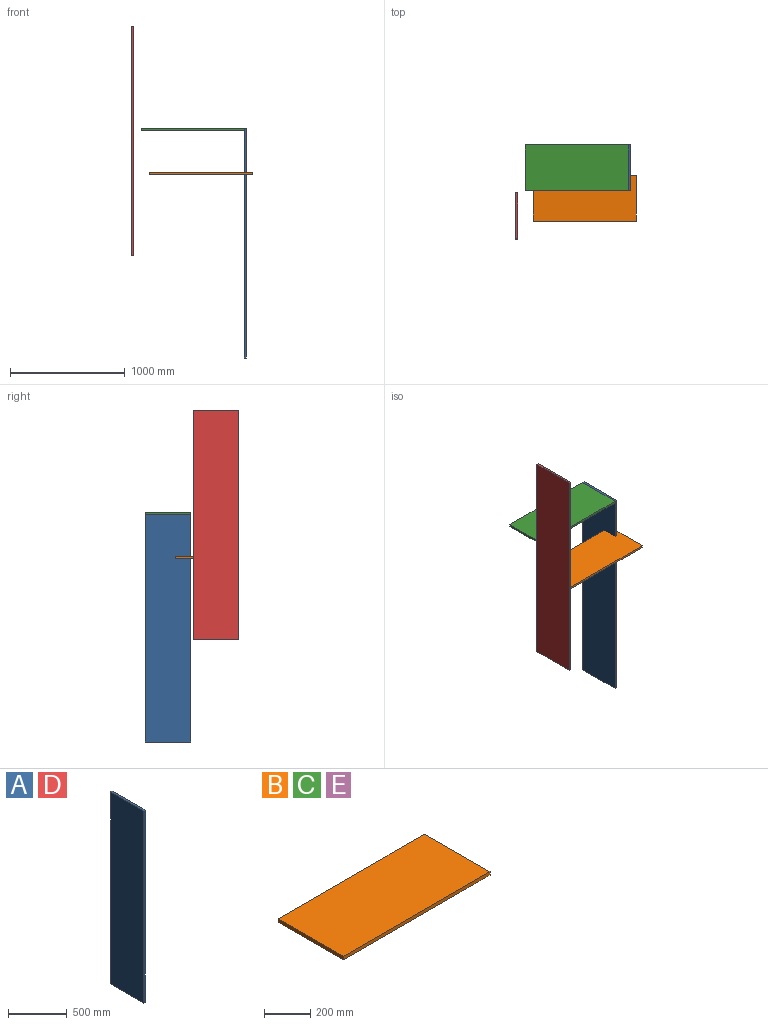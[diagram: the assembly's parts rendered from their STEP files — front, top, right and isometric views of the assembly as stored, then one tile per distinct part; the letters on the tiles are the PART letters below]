
ASSEMBLY  parts=5 mates=1
PART A: 6 faces, bbox 18x400x2000 mm
  f0: plane 2000x400mm, normal (1,0,0), area 800000mm2, adj f1,f3,f4,f5
  f1: plane 400x18mm, normal (0,0,1), area 7200mm2, adj f0,f2,f4,f5
  f2: plane 2000x400mm, normal (-1,0,0), area 800000mm2, adj f1,f3,f4,f5
  f3: plane 400x18mm, normal (0,0,-1), area 7200mm2, adj f0,f2,f4,f5
  f4: plane 2000x18mm, normal (0,-1,0), area 36000mm2, adj f0,f1,f2,f3
  f5: plane 2000x18mm, normal (0,1,0), area 36000mm2, adj f0,f1,f2,f3
PART B: 6 faces, bbox 900x400x18 mm
  f0: plane 900x400mm, normal (0,0,1), area 360000mm2, adj f1,f3,f4,f5
  f1: plane 400x18mm, normal (-1,0,0), area 7200mm2, adj f0,f2,f4,f5
  f2: plane 900x400mm, normal (0,0,-1), area 360000mm2, adj f1,f3,f4,f5
  f3: plane 400x18mm, normal (1,0,0), area 7200mm2, adj f0,f2,f4,f5
  f4: plane 900x18mm, normal (0,-1,0), area 16200mm2, adj f0,f1,f2,f3
  f5: plane 900x18mm, normal (0,1,0), area 16200mm2, adj f0,f1,f2,f3
PART C: same geometry as B
PART D: same geometry as A
PART E: same geometry as B
PLACE A t=(450.7,671.13,-729.78)mm
PLACE B t=(-396.19,407.39,-1108.83)mm
PLACE C t=(-467.3,671.13,-729.78)mm
PLACE D t=(-532.83,252.07,165.03)mm
PLACE E t=(-396.19,407.39,-1108.83)mm
MATE parallel A.f2 <-> C.f3  axis (-1,0,0) through (-17.3,671.13,1042.24)mm
